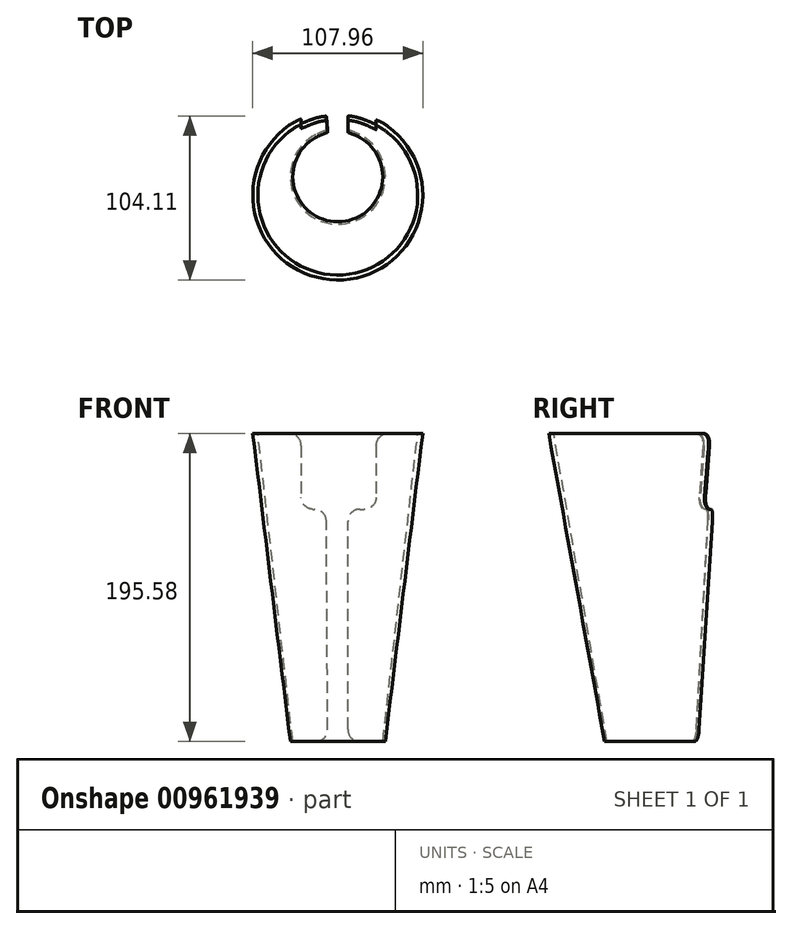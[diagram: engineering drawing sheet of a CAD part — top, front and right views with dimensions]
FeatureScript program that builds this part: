
annotation { "Feature Type Name" : "Feature", "Feature Type Description" : "" }
export const myFeature = defineFeature(function(context is Context, id is Id, definition is map)
    precondition{}
    {
        {
            var Q0;
            Q0=qCreatedBy(makeId("Top.planeOp"),FACE);
            cPlane(context, id + "F0", {"entities" : qUnion([Q0]), "cplaneType" : CPlaneType.OFFSET, "offset" : 195.58 * mm, "width" : 152.4 * mm, "height" : 152.4 * mm});
        }
        {
            var Q0;
            Q0=qCreatedBy(makeId("Top.planeOp"),FACE);
            var sketch = newSketch(context, id + "F1", { "sketchPlane" : qUnion([Q0])});
            skArc(sketch, "E0", {"start": v(-6.35, 27.86) * mm, "mid": v(0, -28.58) * mm, "end": v(6.35, 27.86) * mm});
            skArc(sketch, "E1.0", {"start": v(-6.35, 29.49) * mm, "mid": v(0, -30.16) * mm, "end": v(6.35, 29.49) * mm});
            skLineSegment(sketch, "E2", {"start": v(-6.35, 29.49) * mm, "end": v(-6.35, 27.86) * mm});
            skLineSegment(sketch, "E3", {"start": v(6.35, 29.49) * mm, "end": v(6.35, 27.86) * mm});
            skSolve(sketch);
        }
        {
            var Q0;
            Q0=qCreatedBy(id+"F0.planeOp",FACE);
            var sketch = newSketch(context, id + "F2", { "sketchPlane" : qUnion([Q0])});
            skArc(sketch, "E4", {"start": v(-7.62, 38.62) * mm, "mid": v(0.64, -62.4) * mm, "end": v(6.35, 38.8) * mm});
            skArc(sketch, "E5.0", {"start": v(-7.62, 41.82) * mm, "mid": v(0.64, -65.58) * mm, "end": v(6.35, 42) * mm});
            skLineSegment(sketch, "E6", {"start": v(-7.62, 41.82) * mm, "end": v(-7.62, 38.62) * mm});
            skLineSegment(sketch, "E7", {"start": v(6.35, 42) * mm, "end": v(6.35, 38.8) * mm});
            skSolve(sketch);
        }
        {
            var Q0;
            Q0 = qSketchRegion(id + "F1", true);
            var Q1;
            Q1 = qSketchRegion(id + "F2", true);
            loft(context, id + "F3", {"sheetProfilesArray" : [{ "sheetProfileEntities" : qUnion([Q0]) }, { "sheetProfileEntities" : qUnion([Q1]) }]});
        }
        {
            var Q0;
            Q0=qCreatedBy(makeId("Front.planeOp"),FACE);
            var sketch = newSketch(context, id + "F4", { "sketchPlane" : qUnion([Q0])});
            skLineSegment(sketch, "E8.bottom", {"start": v(-23.22, 213.25) * mm, "end": v(24.43, 213.25) * mm});
            skLineSegment(sketch, "E8.top", {"start": v(-23.22, 147.46) * mm, "end": v(24.43, 147.46) * mm});
            skLineSegment(sketch, "E8.left", {"start": v(-23.22, 213.25) * mm, "end": v(-23.22, 147.46) * mm});
            skLineSegment(sketch, "E8.right", {"start": v(24.43, 213.25) * mm, "end": v(24.43, 147.46) * mm});
            skSolve(sketch);
        }
        {
            var Q0;
            Q0=makeQuery(id+"F4.imprint","IMPRINT",FACE,{"disambiguationData":[TD([[makeQuery(id+"F4.imprint","IMPRINT",EDGE,{"derivedFrom":sQuery(id+"F4.wireOp",EDGE,"E8.bottom")}),-1.0]])]});
            extrude(context, id + "F5", {"entities" : qUnion([Q0]), "operationType" : NewBodyOperationType.REMOVE, "oppositeDirection" : true, "depth" : 508 * mm, "offsetDistance" : 25.4 * mm});
        }
        {
            var Q0;
            Q0=makeQuery(id+"F5.boolean.opBoolean","INTERSECT",EDGE,{"derivedFrom":[makeQuery(id+"F3.opLoft","CAP_FACE",FACE,{"disambiguationData":[OSD([makeQuery(id+"F2.imprint","IMPRINT",FACE,{"disambiguationData":[TD([[makeQuery(id+"F2.imprint","IMPRINT",EDGE,{"derivedFrom":sQuery(id+"F2.wireOp",EDGE,"E4")}),-1.0]])]})])],"isStart":true}),makeQuery(id+"F5.opExtrude","SWEPT_FACE",FACE,{"disambiguationData":[OSD([sQuery(id+"F4.wireOp",EDGE,"E8.right")])]})]});
            var Q1;
            Q1=makeQuery(id+"F5.boolean.opBoolean","COPY",EDGE,{"derivedFrom":makeQuery(id+"F5.opExtrude","SWEPT_EDGE",EDGE,{"disambiguationData":[OSD([sQuery(id+"F4.wireOp",EDGE,"E8.top"),sQuery(id+"F4.wireOp",EDGE,"E8.right")])]})});
            var Q2;
            Q2=makeQuery(id+"F5.boolean.opBoolean","INTERSECT",EDGE,{"derivedFrom":[makeQuery(id+"F3.opLoft","SWEPT_FACE",FACE,{"disambiguationData":[OSD([sQuery(id+"F1.wireOp",EDGE,"E0"),sQuery(id+"F1.wireOp",EDGE,"E1.0"),sQuery(id+"F1.wireOp",EDGE,"E3"),sQuery(id+"F2.wireOp",EDGE,"E4"),sQuery(id+"F2.wireOp",EDGE,"E5.0"),sQuery(id+"F2.wireOp",EDGE,"E7")])]}),makeQuery(id+"F5.opExtrude","SWEPT_FACE",FACE,{"disambiguationData":[OSD([sQuery(id+"F4.wireOp",EDGE,"E8.top")])]})]});
            var Q3;
            Q3=makeQuery(id+"F5.boolean.opBoolean","INTERSECT",EDGE,{"derivedFrom":[makeQuery(id+"F3.opLoft","SWEPT_FACE",FACE,{"disambiguationData":[OSD([sQuery(id+"F1.wireOp",EDGE,"E0"),sQuery(id+"F1.wireOp",EDGE,"E1.0"),sQuery(id+"F1.wireOp",EDGE,"E2"),sQuery(id+"F2.wireOp",EDGE,"E4"),sQuery(id+"F2.wireOp",EDGE,"E5.0"),sQuery(id+"F2.wireOp",EDGE,"E6")])]}),makeQuery(id+"F5.opExtrude","SWEPT_FACE",FACE,{"disambiguationData":[OSD([sQuery(id+"F4.wireOp",EDGE,"E8.top")])]})]});
            var Q4;
            Q4=makeQuery(id+"F5.boolean.opBoolean","COPY",EDGE,{"derivedFrom":makeQuery(id+"F5.opExtrude","SWEPT_EDGE",EDGE,{"disambiguationData":[OSD([sQuery(id+"F4.wireOp",EDGE,"E8.top"),sQuery(id+"F4.wireOp",EDGE,"E8.left")])]})});
            var Q5;
            Q5=makeQuery(id+"F5.boolean.opBoolean","INTERSECT",EDGE,{"derivedFrom":[makeQuery(id+"F3.opLoft","CAP_FACE",FACE,{"disambiguationData":[OSD([makeQuery(id+"F2.imprint","IMPRINT",FACE,{"disambiguationData":[TD([[makeQuery(id+"F2.imprint","IMPRINT",EDGE,{"derivedFrom":sQuery(id+"F2.wireOp",EDGE,"E4")}),-1.0]])]})])],"isStart":true}),makeQuery(id+"F5.opExtrude","SWEPT_FACE",FACE,{"disambiguationData":[OSD([sQuery(id+"F4.wireOp",EDGE,"E8.left")])]})]});
            var Q6;
            Q6=makeQuery(id+"F3.opLoft","MID_CAP_EDGE",EDGE,{"disambiguationData":[OSD([sQuery(id+"F1.wireOp",EDGE,"E0"),sQuery(id+"F1.wireOp",EDGE,"E1.0"),sQuery(id+"F1.wireOp",EDGE,"E3")])],"capPos":0.0});
            var Q7;
            Q7=makeQuery(id+"F3.opLoft","MID_CAP_EDGE",EDGE,{"disambiguationData":[OSD([sQuery(id+"F1.wireOp",EDGE,"E0"),sQuery(id+"F1.wireOp",EDGE,"E1.0"),sQuery(id+"F1.wireOp",EDGE,"E2")])],"capPos":0.0});
            fillet(context, id + "F6", {"entities" : qUnion([Q0, Q1, Q2, Q3, Q4, Q5, Q6, Q7]), "radius" : 7.62 * mm, "tangentPropagation" : true, "allowEdgeOverflow" : false});
        }
    });
